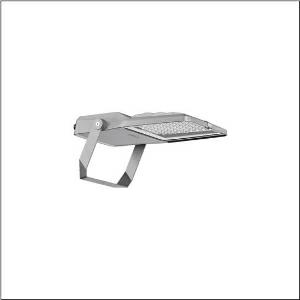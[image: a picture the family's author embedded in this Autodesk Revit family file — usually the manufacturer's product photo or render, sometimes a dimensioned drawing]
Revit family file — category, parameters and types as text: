
# Revit family: floodlight_fl_21_iq_mini___pl33t_5xa7772b2f1a_bcb0
name_source: partatom
category: Lighting Fixtures
units: mm (PartAtom-declared; Revit-internal decimal feet)

## family parameters
Cut with Voids When Loaded = No
Host = Face
Light Source = No
Part Type = Normal
Room Calculation Point = No
Round Connector Dimension = Use Diameter
Shared = No

## types (1)
- --- (1 x LED, 6170 lm, 45.5 W, 3000K)
    Apparent Load = 46 VA
    CIE Flux Codes = 26 75 99 100 100
    Color Rendering = 70
    Color Temperature = 3000K
    Default Elevation = 1800 mm
    Description = Floodlight FL 21 iQ mini, floodlight, primary light control with lens, of PMMA, primary optical cover: protective disc, of toughened safety glass, transparent, light distribution: PL33T, light emission: direct distribution, installation type: surface-mounted, LED, High Power LED, rated luminous flux: 6.170lm, luminous efficacy: 136lm/W, light colour: 730, colour temperature: 3000K, control gear: iQ Street-Remote/DALI, control: Street-Remote, Auto-Match, Temp-Guard, Night-Set, Smart-Wire, Desk-Remote (wireless, voltage-free reading and setting of iQ features in the workshop via application-optimized NFC function/RFID function), optimised constant luminous flux control (CLO 2.0), with terminal, 6-pole, mains connection: 220..240V, AC, 50/60Hz, start of lifetime: 46W, end of service life: 48W, reduction: 22W, luminaire housing, of diecast aluminium, powder-coated, Siteco® metallic grey (DB 702S), corrosivity category C5 mid according to DIN EN ISO 12944, suitable for swimming pools, chlorine-resistant, sealing non-destructively replaceable, mounting bracket, of steel, galvanised, powder-coated, Siteco® metallic grey (DB 702S), protection rating (complete): IP66, insulation class (complete): insulation class II (safety insulation), certification: CE, ENEC, VDE, protection symbol: D, impact resistance: IK08, permissible operating ambient temperature: -40..+40°C, permissible operating ambient temperature for outdoor applications: -40..+50°C, standard: DIN EN 12944, LABS conformity tested according to VDMA 24364:2018-05, packaging unit: 1 piece

Light Distribution: PL33T
    Height = 70 mm
    Lamp = 1 x LED
    Lamp Light Flux = 6170 lm
    Lamp Power = 45.5 W
    Lamp count = 1
    Length = 485 mm
    Luminous efficacy = 136 lm/W
    Manufacturer = Siteco
    ModVariant = No
    Model = 5XA7772B2F1A
    Number of Poles = 1
    OnlyDefault = Yes
    Power Factor = 1
    Product Name = Floodlight FL 21 iQ mini | PL33T
    Product group = floodlight | pylon annexe
    ProductGroupID = 6200
    Protection Class = Protection class II
    Protection Degree = IP 66
    RLX_Detail_Level = 1
    RLX_Emergency_Light_Flux = 0 lm
    RLX_Emergency_Type = 0
    RLX_Emergency_Type_DB = No
    RlxData = <blob elided: 96145 chars, md5=dfc131a9>
    Socket = socket
    Standby Power = 0 W
    System Light Flux = 6170 lm
    System Power = 46 W
    Type Comments = factory setting: luminous flux: 100 % | dim-lin: 254 | 463 mA
    Type Image = l_1006845.jpg
    URL = http://relux.com
    VarID = @adj_150104
    Voltage = 0 V
    Weight = 0.00 kg
    Width = 337 mm

## geometry (parser evidence)
native form markers: Blend x4, Sweep x11
no freeform markers — native parametric forms only
